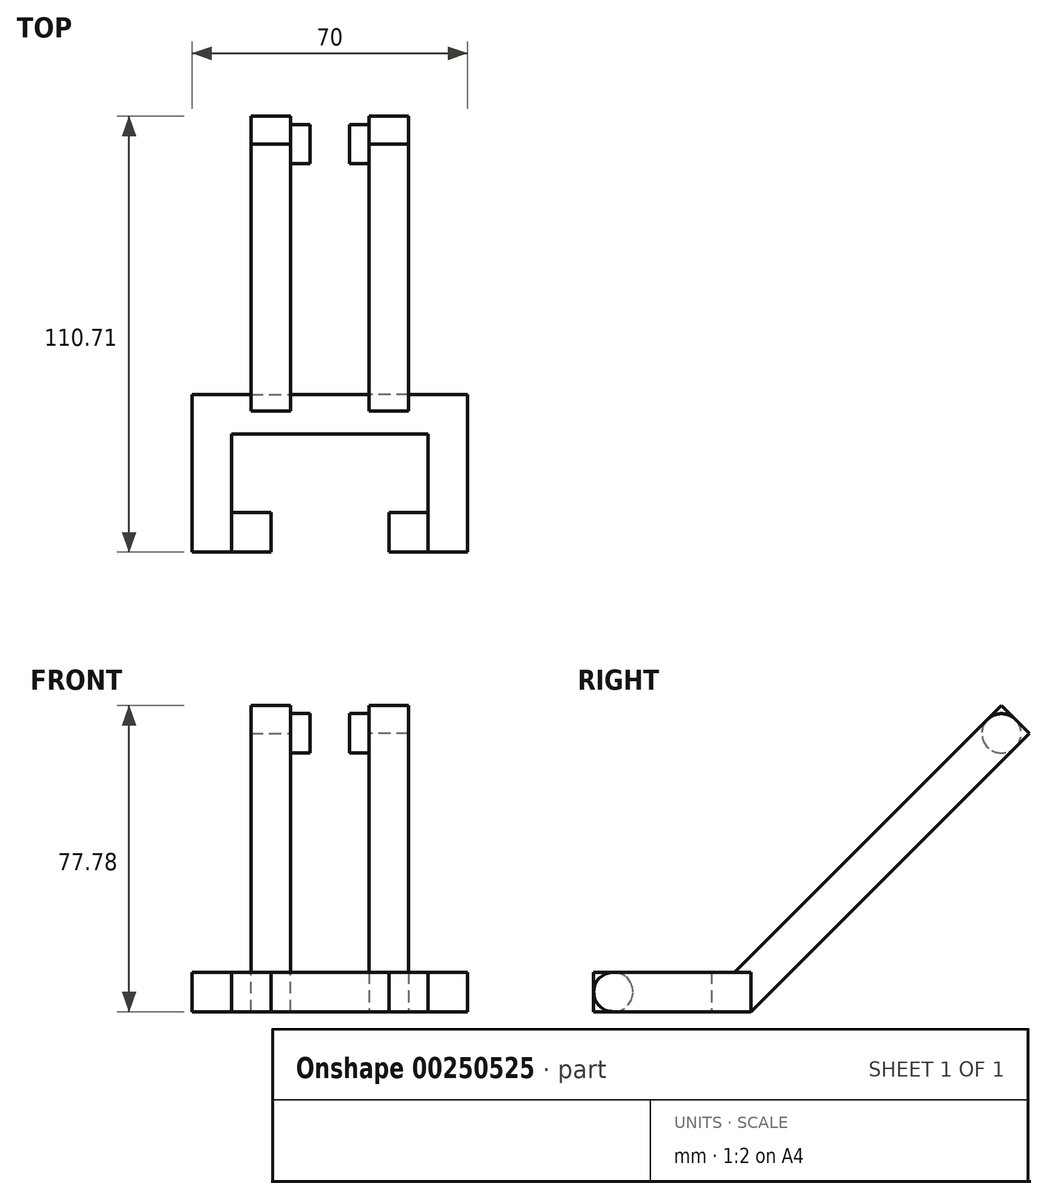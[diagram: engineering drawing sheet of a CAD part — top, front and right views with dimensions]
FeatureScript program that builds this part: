
annotation { "Feature Type Name" : "Feature", "Feature Type Description" : "" }
export const myFeature = defineFeature(function(context is Context, id is Id, definition is map)
    precondition{}
    {
        {
            var Q0;
            Q0=qCreatedBy(makeId("Top.planeOp"),FACE);
            var sketch = newSketch(context, id + "F0", { "sketchPlane" : qUnion([Q0])});
            skLineSegment(sketch, "E0", {"start": v(-25, -18.61) * mm, "end": v(-35, -18.61) * mm});
            skLineSegment(sketch, "E1", {"start": v(-35, -18.61) * mm, "end": v(-35, 21.39) * mm});
            skLineSegment(sketch, "E2", {"start": v(-35, 21.39) * mm, "end": v(35, 21.39) * mm});
            skLineSegment(sketch, "E3", {"start": v(35, 21.39) * mm, "end": v(35, -18.61) * mm});
            skLineSegment(sketch, "E4", {"start": v(35, -18.61) * mm, "end": v(25, -18.61) * mm});
            skLineSegment(sketch, "E5", {"start": v(25, -8.61) * mm, "end": v(25, 11.39) * mm});
            skLineSegment(sketch, "E6", {"start": v(25, 11.39) * mm, "end": v(-25, 11.39) * mm});
            skLineSegment(sketch, "E7", {"start": v(-25, 11.39) * mm, "end": v(-25, -8.61) * mm});
            skLineSegment(sketch, "E8", {"start": v(25, -8.61) * mm, "end": v(25, -18.61) * mm});
            skLineSegment(sketch, "E9", {"start": v(-25, -8.61) * mm, "end": v(-25, -18.61) * mm});
            skPoint(sketch, "E10.orphan", {"position": v(15, -18.61) * mm});
            skSolve(sketch);
        }
        {
            var Q0;
            Q0 = qSketchRegion(id + "F0", true);
            extrude(context, id + "F1", {"entities" : qUnion([Q0]), "depth" : 10 * mm});
        }
        {
            var Q0;
            Q0=makeQuery(id+"F1.opExtrude","SWEPT_FACE",FACE,{"disambiguationData":[OSD([sQuery(id+"F0.wireOp",EDGE,"E7"),sQuery(id+"F0.wireOp",EDGE,"E9")])]});
            var sketch = newSketch(context, id + "F2", { "sketchPlane" : qUnion([Q0])});
            skCircle(sketch, "E11", {"center": v(-13.58, 5) * mm, "radius": 5 * mm});
            skPoint(sketch, "E11.centerSnap0", {"position": v(-18.61, 5) * mm});
            skSolve(sketch);
        }
        {
            var Q0;
            Q0 = qSketchRegion(id + "F2", true);
            extrude(context, id + "F3", {"entities" : qUnion([Q0]), "depth" : 10 * mm});
        }
        {
            var Q0;
            Q0=makeQuery(id+"F3.opExtrude","SWEPT_BODY",BODY,{"disambiguationData":[OSD([sQuery(id+"F2.wireOp",EDGE,"E11")])]});
            var Q1;
            Q1=qCreatedBy(makeId("Right.planeOp"),FACE);
            mirror(context, id + "F4", {"operationType" : NewBodyOperationType.ADD, "entities" : qUnion([Q0]), "mirrorPlane" : qUnion([Q1])});
        }
        {
            var Q0;
            Q0=qCreatedBy(makeId("Right.planeOp"),FACE);
            cPlane(context, id + "F5", {"entities" : qUnion([Q0]), "cplaneType" : CPlaneType.OFFSET, "offset" : 10 * mm, "width" : 150 * mm, "height" : 150 * mm});
        }
        {
            var Q0;
            Q0=qCreatedBy(id+"F5.planeOp",FACE);
            var sketch = newSketch(context, id + "F6", { "sketchPlane" : qUnion([Q0])});
            skLineSegment(sketch, "E12", {"start": v(21.39, 0) * mm, "end": v(92.1, 70.71) * mm});
            skLineSegment(sketch, "E13", {"start": v(14.32, 7.07) * mm, "end": v(85.03, 77.78) * mm});
            skLineSegment(sketch, "E14", {"start": v(0, 0) * mm, "end": v(43.83, 0) * mm, "construction": true});
            skLineSegment(sketch, "E15", {"start": v(14.32, 7.07) * mm, "end": v(21.39, 0) * mm});
            skLineSegment(sketch, "E16", {"start": v(85.03, 77.78) * mm, "end": v(92.1, 70.71) * mm});
            skSolve(sketch);
        }
        {
            var Q0;
            Q0 = qSketchRegion(id + "F6", true);
            extrude(context, id + "F7", {"entities" : qUnion([Q0]), "depth" : 10 * mm});
        }
        {
            var Q0;
            Q0=makeQuery(id+"F7.opExtrude","CAP_FACE",FACE,{"disambiguationData":[OSD([sQuery(id+"F6.wireOp",EDGE,"E12"),sQuery(id+"F6.wireOp",EDGE,"E13"),sQuery(id+"F6.wireOp",EDGE,"E15"),sQuery(id+"F6.wireOp",EDGE,"E16")])],"isStart":true});
            var sketch = newSketch(context, id + "F8", { "sketchPlane" : qUnion([Q0])});
            skCircle(sketch, "E17", {"center": v(-85.03, 70.71) * mm, "radius": 5 * mm});
            skSolve(sketch);
        }
        {
            var Q0;
            Q0 = qSketchRegion(id + "F8", true);
            extrude(context, id + "F9", {"entities" : qUnion([Q0]), "operationType" : NewBodyOperationType.ADD, "depth" : 5 * mm});
        }
        {
            var Q0;
            Q0=makeQuery(id+"F7.opExtrude","SWEPT_BODY",BODY,{"disambiguationData":[OSD([sQuery(id+"F6.wireOp",EDGE,"E12"),sQuery(id+"F6.wireOp",EDGE,"E13"),sQuery(id+"F6.wireOp",EDGE,"E15"),sQuery(id+"F6.wireOp",EDGE,"E16")])]});
            var Q1;
            Q1=qCreatedBy(makeId("Right.planeOp"),FACE);
            mirror(context, id + "F10", {"operationType" : NewBodyOperationType.ADD, "entities" : qUnion([Q0]), "mirrorPlane" : qUnion([Q1])});
        }
    });
